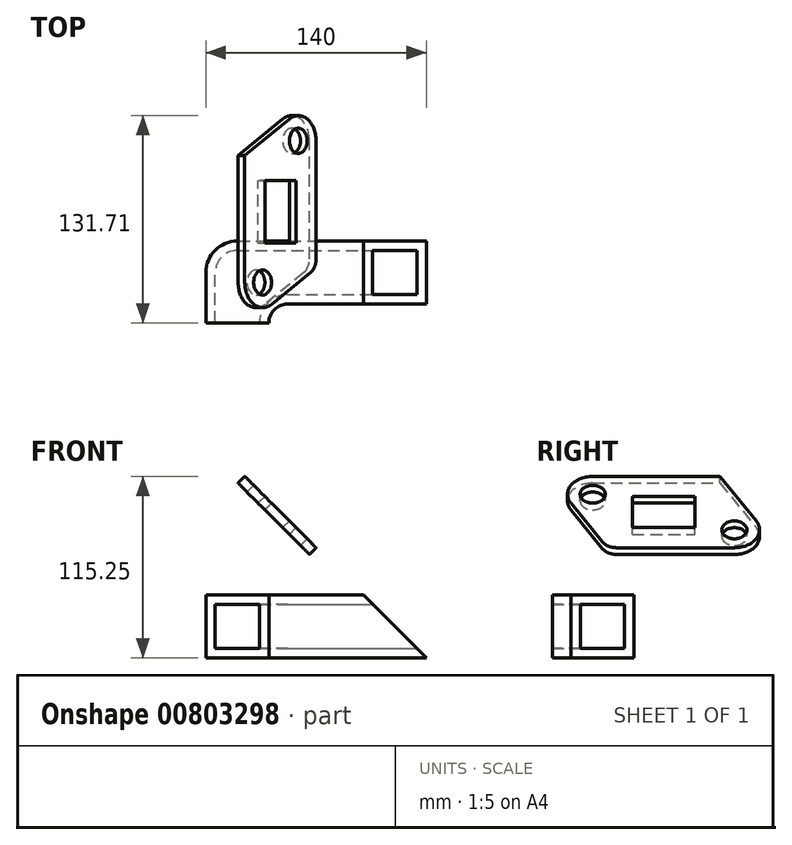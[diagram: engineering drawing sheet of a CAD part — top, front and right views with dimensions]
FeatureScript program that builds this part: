
annotation { "Feature Type Name" : "Feature", "Feature Type Description" : "" }
export const myFeature = defineFeature(function(context is Context, id is Id, definition is map)
    precondition{}
    {
        {
            var Q0;
            Q0=qCreatedBy(makeId("Top.planeOp"),FACE);
            var sketch = newSketch(context, id + "F0", { "sketchPlane" : qUnion([Q0])});
            skLineSegment(sketch, "E0", {"start": v(0, 0) * mm, "end": v(0, 32) * mm, "construction": true});
            skLineSegment(sketch, "E1", {"start": v(-20, 0) * mm, "end": v(20, 0) * mm});
            skArc(sketch, "E2", {"start": v(32, 12) * mm, "mid": v(23.51, 8.49) * mm, "end": v(20, 0) * mm});
            skLineSegment(sketch, "E3", {"start": v(32, 12) * mm, "end": v(120, 12) * mm});
            skLineSegment(sketch, "E4", {"start": v(-20, 0) * mm, "end": v(-20, 32) * mm});
            skLineSegment(sketch, "E5", {"start": v(0, 52) * mm, "end": v(80, 52) * mm});
            skLineSegment(sketch, "E6", {"start": v(32, 12) * mm, "end": v(32, 52) * mm, "construction": true});
            skLineSegment(sketch, "E7", {"start": v(-20, 32) * mm, "end": v(100, 32) * mm, "construction": true});
            skPoint(sketch, "E7.startSnap0", {"position": v(32, 32) * mm});
            skPoint(sketch, "E8.visualSharp", {"position": v(-20, 52) * mm});
            skArc(sketch, "E8.filletArc", {"start": v(0, 52) * mm, "mid": v(-14.14, 46.14) * mm, "end": v(-20, 32) * mm});
            skLineSegment(sketch, "E9", {"start": v(120, 12) * mm, "end": v(80, 52) * mm});
            skLineSegment(sketch, "E10", {"start": v(80, 52) * mm, "end": v(120, 52) * mm});
            skLineSegment(sketch, "E11", {"start": v(120, 52) * mm, "end": v(120, 12) * mm});
            skSolve(sketch);
        }
        {
            var Q0;
            Q0=makeQuery(id+"F0.imprint","IMPRINT",FACE,{"disambiguationData":[TD([[makeQuery(id+"F0.imprint","IMPRINT",EDGE,{"derivedFrom":sQuery(id+"F0.wireOp",EDGE,"E1")}),1.0]])]});
            var Q1;
            Q1=makeQuery(id+"F0.imprint","IMPRINT",FACE,{"disambiguationData":[TD([[makeQuery(id+"F0.imprint","IMPRINT",EDGE,{"derivedFrom":sQuery(id+"F0.wireOp",EDGE,"E9")}),-1.0]])]});
            extrude(context, id + "F1", {"entities" : qUnion([Q0, Q1]), "depth" : 40 * mm, "offsetDistance" : 25 * mm, "symmetric" : true});
        }
        {
            var Q0;
            Q0=makeQuery(id+"F1.opExtrude","SWEPT_FACE",FACE,{"disambiguationData":[OSD([sQuery(id+"F0.wireOp",EDGE,"E1")])]});
            var Q1;
            Q1=makeQuery(id+"F1.opExtrude","SWEPT_FACE",FACE,{"disambiguationData":[OSD([sQuery(id+"F0.wireOp",EDGE,"E11")])]});
            shell(context, id + "F2", {"entities" : qUnion([Q0, Q1]), "thickness" : ((40 - 28) / 2) * mm});
        }
        {
            var Q0;
            Q0=makeQuery(id+"F1.opExtrude","SWEPT_FACE",FACE,{"disambiguationData":[OSD([sQuery(id+"F0.wireOp",EDGE,"E3")])]});
            var sketch = newSketch(context, id + "F3", { "sketchPlane" : qUnion([Q0])});
            skLineSegment(sketch, "E12.0", {"start": v(-20, 0) * mm, "end": v(100, 0) * mm, "construction": true});
            skLineSegment(sketch, "E13", {"start": v(120, -20) * mm, "end": v(80, 20) * mm});
            skLineSegment(sketch, "E14.0", {"start": v(32, 20) * mm, "end": v(120, 20) * mm});
            skLineSegment(sketch, "E15.0", {"start": v(120, 20) * mm, "end": v(120, -20) * mm});
            skSolve(sketch);
        }
        {
            var Q0;
            Q0 = qSketchRegion(id + "F3", true);
            extrude(context, id + "F4", {"entities" : qUnion([Q0]), "operationType" : NewBodyOperationType.REMOVE, "endBound" : BoundingType.THROUGH_ALL, "oppositeDirection" : true, "depth" : 25 * mm, "offsetDistance" : 25 * mm});
        }
        {
            var Q0;
            Q0=makeQuery(id+"F4.boolean.opBoolean","COPY",FACE,{"derivedFrom":makeQuery(id+"F4.opExtrude","SWEPT_FACE",FACE,{"disambiguationData":[OSD([sQuery(id+"F3.wireOp",EDGE,"E13")])]})});
            var sketch = newSketch(context, id + "F5", { "sketchPlane" : qUnion([Q0])});
            skLineSegment(sketch, "E16.0", {"start": v(50.91, 46) * mm, "end": v(90.5, 46) * mm});
            skLineSegment(sketch, "E17", {"start": v(50.91, 32) * mm, "end": v(70.71, 32) * mm, "construction": true});
            skPoint(sketch, "E17.endSnap0", {"position": v(70.71, 46) * mm});
            skLineSegment(sketch, "E18", {"start": v(70.71, 32) * mm, "end": v(70.71, 46) * mm, "construction": true});
            skLineSegment(sketch, "E19.0", {"start": v(50.91, 18) * mm, "end": v(50.91, 46) * mm});
            skLineSegment(sketch, "E20.0", {"start": v(50.91, 18) * mm, "end": v(90.5, 18) * mm});
            skLineSegment(sketch, "E21.0", {"start": v(90.5, 18) * mm, "end": v(90.5, 46) * mm});
            skCircle(sketch, "E22", {"center": v(25.71, 48) * mm, "radius": 8 * mm});
            skArc(sketch, "E23", {"start": v(25.71, 64) * mm, "mid": v(11.85, 56) * mm, "end": v(11.85, 40) * mm});
            skLineSegment(sketch, "E24", {"start": v(25.71, 64) * mm, "end": v(106.47, 64) * mm});
            skLineSegment(sketch, "E25.MirrorCS", {"start": v(40.72, 0) * mm, "end": v(115.71, 0) * mm});
            skLineSegment(sketch, "E26", {"start": v(32.06, 5) * mm, "end": v(11.85, 40) * mm});
            skPoint(sketch, "E27.orphan", {"position": v(25.71, 0) * mm});
            skPoint(sketch, "E28.visualSharp", {"position": v(34.95, 0) * mm});
            skArc(sketch, "E28.filletArc", {"start": v(32.06, 5) * mm, "mid": v(35.72, 1.34) * mm, "end": v(40.72, 0) * mm});
            skCircle(sketch, "E29", {"center": v(115.71, 16) * mm, "radius": 8 * mm});
            skArc(sketch, "E30", {"start": v(115.71, 0) * mm, "mid": v(129.57, 8) * mm, "end": v(129.57, 24) * mm});
            skPoint(sketch, "E31.orphan", {"position": v(70.71, 0) * mm});
            skPoint(sketch, "E32.orphan", {"position": v(70.71, 64) * mm});
            skLineSegment(sketch, "E33", {"start": v(106.47, 64) * mm, "end": v(129.57, 24) * mm});
            skSolve(sketch);
        }
        {
            var Q0;
            Q0 = qSketchRegion(id + "F5", true);
            extrude(context, id + "F6", {"entities" : qUnion([Q0]), "operationType" : NewBodyOperationType.ADD, "oppositeDirection" : true, "depth" : 6 * mm, "offsetDistance" : 25 * mm});
        }
        {
            var Q0;
            Q0=qCreatedBy(makeId("Right.planeOp"),FACE);
            var sketch = newSketch(context, id + "F7", { "sketchPlane" : qUnion([Q0])});
            skLineSegment(sketch, "E34.0", {"start": v(18, 14) * mm, "end": v(46, 14) * mm});
            skLineSegment(sketch, "E35.0", {"start": v(46, 14) * mm, "end": v(46, -14) * mm});
            skLineSegment(sketch, "E36.0", {"start": v(18, -14) * mm, "end": v(46, -14) * mm});
            skLineSegment(sketch, "E37.0", {"start": v(18, 14) * mm, "end": v(18, -14) * mm});
            skSolve(sketch);
        }
        {
            var Q0;
            Q0 = qSketchRegion(id + "F7", true);
            extrude(context, id + "F8", {"entities" : qUnion([Q0]), "operationType" : NewBodyOperationType.REMOVE, "endBound" : BoundingType.THROUGH_ALL, "depth" : 25 * mm, "offsetDistance" : 25 * mm});
        }
    });
